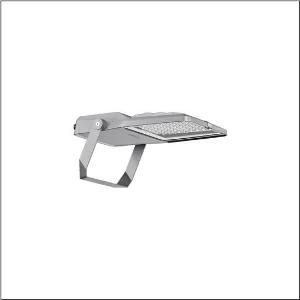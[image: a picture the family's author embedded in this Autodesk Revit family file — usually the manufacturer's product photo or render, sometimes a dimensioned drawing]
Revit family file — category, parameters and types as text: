
# Revit family: floodlight_fl_21_iq_mini___pl43_5xa7772b1a1a_21a9
name_source: partatom
category: Lighting Fixtures
units: mm (PartAtom-declared; Revit-internal decimal feet)

## family parameters
Cut with Voids When Loaded = No
Host = Face
Light Source = No
Part Type = Normal
Room Calculation Point = No
Round Connector Dimension = Use Diameter
Shared = No

## types (1)
- --- (1 x LED, 5300 lm, 45.5 W, 2200K)
    Apparent Load = 46 VA
    CIE Flux Codes = 27 78 99 100 100
    Color Rendering = 70
    Color Temperature = 2200K
    Default Elevation = 1800 mm
    Description = Floodlight FL 21 iQ mini, floodlight, primary light control with lens, of PMMA, primary optical cover: protective disc, of toughened safety glass, transparent, light distribution: PL43, light emission: direct distribution, installation type: surface-mounted, LED, High Power LED, rated luminous flux: 5.300lm, luminous efficacy: 117lm/W, light colour: 722, colour temperature: 2200K, control: Street-Remote, Auto-Match, Temp-Guard, Night-Set, Smart-Wire, Desk-Remote (wireless, voltage-free reading and setting of iQ features in the workshop via application-optimized NFC function/RFID function), optimised constant luminous flux control (CLO 2.0), with terminal, 6-pole, mains connection: 220..240V, AC, 50/60Hz, start of lifetime: 46W, end of service life: 48W, reduction: 21W, luminaire housing, of diecast aluminium, powder-coated, Siteco® metallic grey (DB 702S), corrosivity category C5 mid according to DIN EN ISO 12944, sealing non-destructively replaceable, mounting bracket, of steel, galvanised, powder-coated, Siteco® metallic grey (DB 702S), protection rating (complete): IP66, insulation class (complete): insulation class II (safety insulation), certification: CE, ENEC, VDE, protection symbol: D, impact resistance: IK08, permissible operating ambient temperature: -40..+40°C, permissible operating ambient temperature for outdoor applications: -40..+50°C, standard: DIN EN 12944, LABS conformity tested according to VDMA 24364:2018-05, packaging unit: 1 piece

Light Distribution: PL43
    Height = 70 mm
    Lamp = 1 x LED
    Lamp Light Flux = 5300 lm
    Lamp Power = 45.5 W
    Lamp count = 1
    Length = 485 mm
    Luminous efficacy = 116 lm/W
    Manufacturer = Siteco
    ModVariant = No
    Model = 5XA7772B1A1A
    Number of Poles = 1
    OnlyDefault = Yes
    Power Factor = 1
    Product Name = Floodlight FL 21 iQ mini | PL43
    Product group = floodlight | pylon annexe
    ProductGroupID = 6200
    Protection Class = Protection class II
    Protection Degree = IP 66
    RLX_Detail_Level = 1
    RLX_Emergency_Light_Flux = 0 lm
    RLX_Emergency_Type = 0
    RLX_Emergency_Type_DB = No
    RlxData = <blob elided: 95837 chars, md5=69f93222>
    Socket = socket
    Standby Power = 0 W
    System Light Flux = 5300 lm
    System Power = 46 W
    Type Comments = factory setting: luminous flux: 100 % | dim-lin: 254 | 463 mA
    Type Image = l_1006845.jpg
    URL = http://relux.com
    VarID = @adj_095161
    Voltage = 0 V
    Weight = 0.00 kg
    Width = 337 mm

## geometry (parser evidence)
native form markers: Blend x4, Sweep x14
no freeform markers — native parametric forms only
